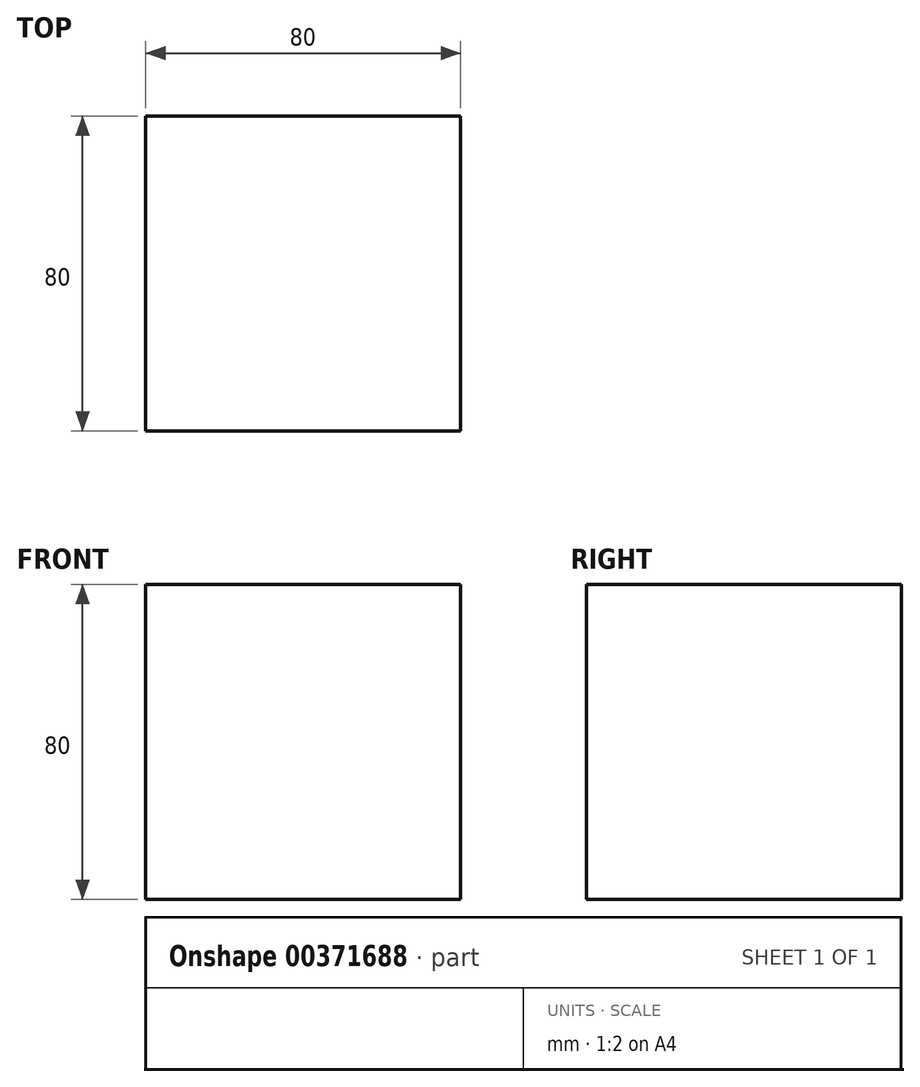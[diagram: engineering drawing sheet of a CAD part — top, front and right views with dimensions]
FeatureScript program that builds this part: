
annotation { "Feature Type Name" : "Feature", "Feature Type Description" : "" }
export const myFeature = defineFeature(function(context is Context, id is Id, definition is map)
    precondition{}
    {
        {
            var Q0;
            Q0=qCreatedBy(makeId("Top.planeOp"),FACE);
            var sketch = newSketch(context, id + "F0", { "sketchPlane" : qUnion([Q0])});
            skLineSegment(sketch, "E0.bottom", {"start": v(-40, 40) * mm, "end": v(40, 40) * mm});
            skLineSegment(sketch, "E0.top", {"start": v(-40, -40) * mm, "end": v(40, -40) * mm});
            skLineSegment(sketch, "E0.left", {"start": v(-40, 40) * mm, "end": v(-40, -40) * mm});
            skLineSegment(sketch, "E0.right", {"start": v(40, 40) * mm, "end": v(40, -40) * mm});
            skPoint(sketch, "E0.middle", {"position": v(0, 0) * mm});
            skSolve(sketch);
        }
        {
            var Q0;
            Q0=makeQuery(id+"F0.imprint","IMPRINT",FACE,{"disambiguationData":[TD([[makeQuery(id+"F0.imprint","IMPRINT",EDGE,{"derivedFrom":sQuery(id+"F0.wireOp",EDGE,"E0.bottom")}),-1.0]])]});
            extrude(context, id + "F1", {"entities" : qUnion([Q0]), "depth" : 80 * mm});
        }
    });
